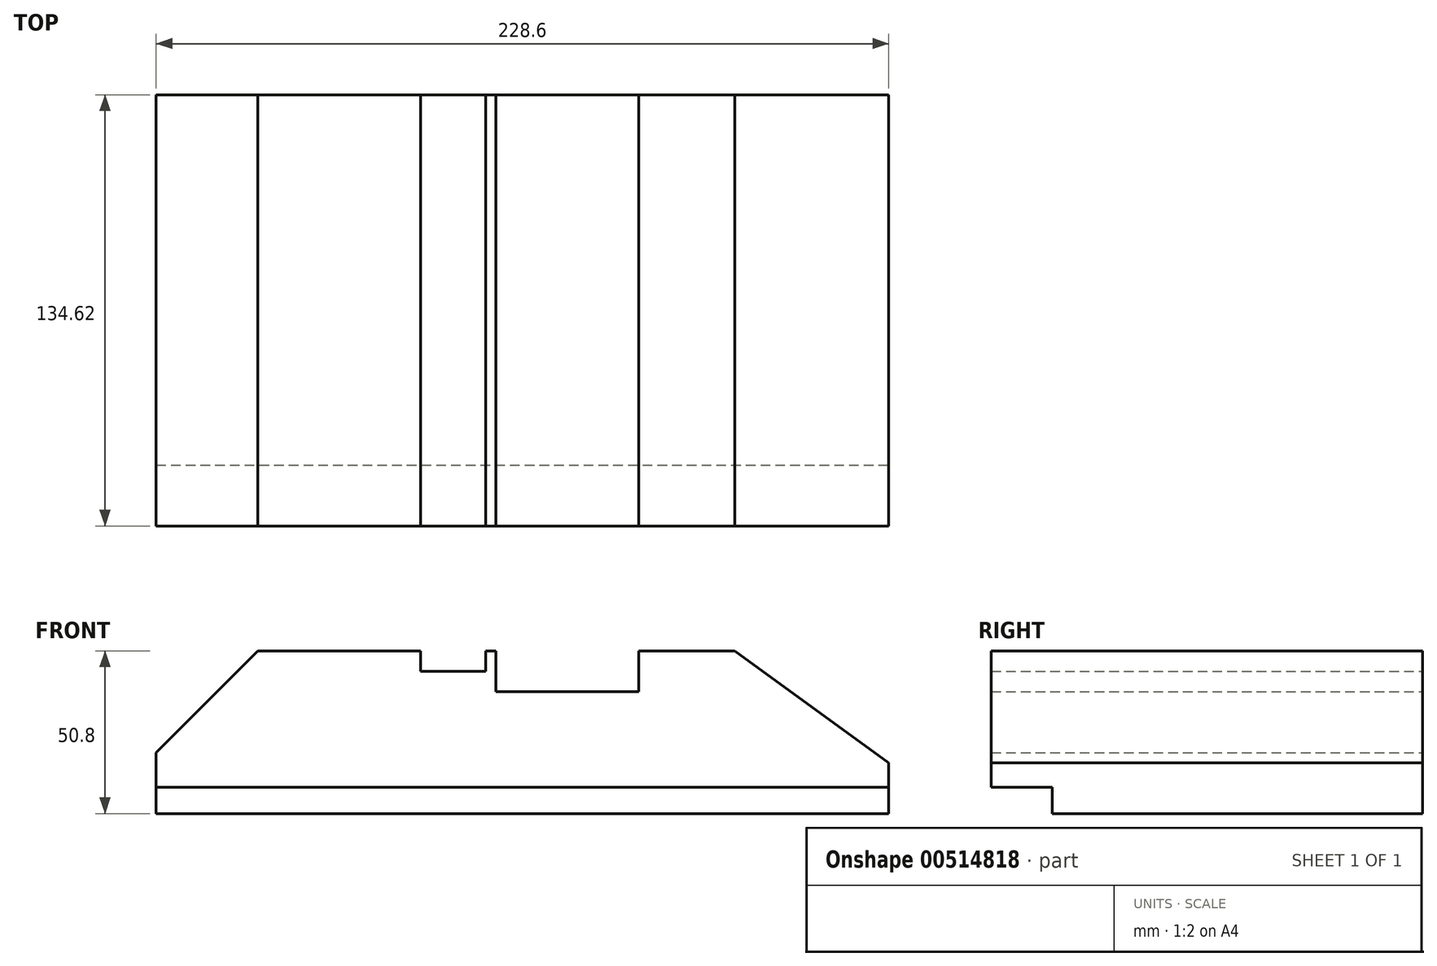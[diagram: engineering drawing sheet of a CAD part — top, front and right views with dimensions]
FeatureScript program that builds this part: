
annotation { "Feature Type Name" : "Feature", "Feature Type Description" : "" }
export const myFeature = defineFeature(function(context is Context, id is Id, definition is map)
    precondition{}
    {
        {
            var Q0;
            Q0=qCreatedBy(makeId("Front.planeOp"),FACE);
            var sketch = newSketch(context, id + "F0", { "sketchPlane" : qUnion([Q0])});
            skLineSegment(sketch, "E0.bottom", {"start": v(114.3, -25.4) * mm, "end": v(-114.3, -25.4) * mm});
            skLineSegment(sketch, "E0.top", {"start": v(66.3, 25.4) * mm, "end": v(36.2, 25.4) * mm});
            skLineSegment(sketch, "E0.left", {"start": v(114.3, -25.4) * mm, "end": v(114.3, -9.52) * mm});
            skLineSegment(sketch, "E0.right", {"start": v(-114.3, -25.4) * mm, "end": v(-114.3, -6.35) * mm});
            skPoint(sketch, "E0.middle", {"position": v(0, 0) * mm});
            skLineSegment(sketch, "E1", {"start": v(-82.55, 25.4) * mm, "end": v(-114.3, -6.35) * mm});
            skPoint(sketch, "E2.orphan", {"position": v(-114.3, 25.4) * mm});
            skLineSegment(sketch, "E3", {"start": v(66.3, 25.4) * mm, "end": v(114.3, -9.52) * mm});
            skPoint(sketch, "E4.orphan", {"position": v(114.3, 25.4) * mm});
            skPoint(sketch, "E5.start.orphan", {"position": v(-82.55, 34.54) * mm});
            skLineSegment(sketch, "E6", {"start": v(-31.75, 25.4) * mm, "end": v(-31.75, 19.05) * mm});
            skLineSegment(sketch, "E7", {"start": v(-31.75, 19.05) * mm, "end": v(-11.43, 19.05) * mm});
            skLineSegment(sketch, "E8", {"start": v(-11.43, 19.05) * mm, "end": v(-11.43, 25.4) * mm});
            skLineSegment(sketch, "E9.trimOffspring", {"start": v(-31.75, 25.4) * mm, "end": v(-82.55, 25.4) * mm});
            skLineSegment(sketch, "E10", {"start": v(36.2, 25.4) * mm, "end": v(36.2, 12.7) * mm});
            skLineSegment(sketch, "E11", {"start": v(36.2, 12.7) * mm, "end": v(-8.26, 12.7) * mm});
            skLineSegment(sketch, "E12", {"start": v(-8.26, 12.7) * mm, "end": v(-8.26, 25.4) * mm});
            skLineSegment(sketch, "E13.trimOffspring", {"start": v(-8.26, 25.4) * mm, "end": v(-11.43, 25.4) * mm});
            skPoint(sketch, "E14.start.orphan", {"position": v(-11.43, 31.95) * mm});
            skPoint(sketch, "E15.start.orphan", {"position": v(-8.26, 31.95) * mm});
            skSolve(sketch);
        }
        {
            var Q0;
            Q0=makeQuery(id+"F0.imprint","IMPRINT",FACE,{"disambiguationData":[TD([[makeQuery(id+"F0.imprint","IMPRINT",EDGE,{"derivedFrom":sQuery(id+"F0.wireOp",EDGE,"E0.bottom")}),-1.0]])]});
            extrude(context, id + "F1", {"entities" : qUnion([Q0]), "depth" : 134.62 * mm, "offsetDistance" : 25.4 * mm});
        }
        {
            var Q0;
            Q0=makeQuery(id+"F1.opExtrude","SWEPT_FACE",FACE,{"disambiguationData":[OSD([sQuery(id+"F0.wireOp",EDGE,"E0.left")])]});
            var sketch = newSketch(context, id + "F2", { "sketchPlane" : qUnion([Q0])});
            skLineSegment(sketch, "E16.0", {"start": v(-134.62, -17.15) * mm, "end": v(-115.57, -17.15) * mm});
            skLineSegment(sketch, "E17.0", {"start": v(-115.57, -25.4) * mm, "end": v(-115.57, -17.15) * mm});
            skLineSegment(sketch, "E18.0", {"start": v(6.35, -31.75) * mm, "end": v(6.35, -3.17) * mm});
            skLineSegment(sketch, "E18.1", {"start": v(-140.97, -31.75) * mm, "end": v(6.35, -31.75) * mm});
            skLineSegment(sketch, "E18.2", {"start": v(-140.97, -3.17) * mm, "end": v(-140.97, -31.75) * mm});
            skLineSegment(sketch, "E18.3", {"start": v(6.35, -3.17) * mm, "end": v(-140.97, -3.17) * mm});
            skSolve(sketch);
        }
        {
            var Q0;
            {var subQ0=sQuery(id+"F2.wireOp",EDGE,"E16.0");Q0=makeQuery(id+"F2.imprint","IMPRINT",FACE,{"disambiguationData":[TD([[makeQuery(id+"F2.imprint","IMPRINT",EDGE,{"derivedFrom":subQ0}),-1.0]])]});}
            extrude(context, id + "F3", {"entities" : qUnion([Q0]), "operationType" : NewBodyOperationType.REMOVE, "oppositeDirection" : true, "depth" : 228.6 * mm, "offsetDistance" : 25.4 * mm});
        }
    });
